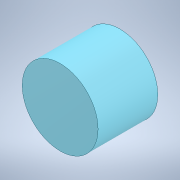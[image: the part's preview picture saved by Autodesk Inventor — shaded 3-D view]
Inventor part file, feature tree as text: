
AUTODESK INVENTOR PART (.ipt)
format: ipt  version: 2022 (Build 260153000, 153)  size: 98,304 bytes
history: native  units: in
note: dims shown in document units (in); Inventor stores cm internally (conversion verified against a paired STEP export)
features: extrude x1, sketch x1
ambient origin geometry x8: Origin, YZ Plane, XZ Plane, XY Plane, X Axis, Y Axis, Z Axis, Center Point
bodies: Solid1 (feature_tree)
feature tree (2):
  extrude  "Extrusion1"  [1 undecoded]
  sketch  "Sketch2"  dims[d0=0.1969in d1=0.0in]
note: 1 required parameter value undecoded (feature->parameter linkage not recoverable at this tier; creation-order binding heuristic only, values carry confidence <= 0.55)
